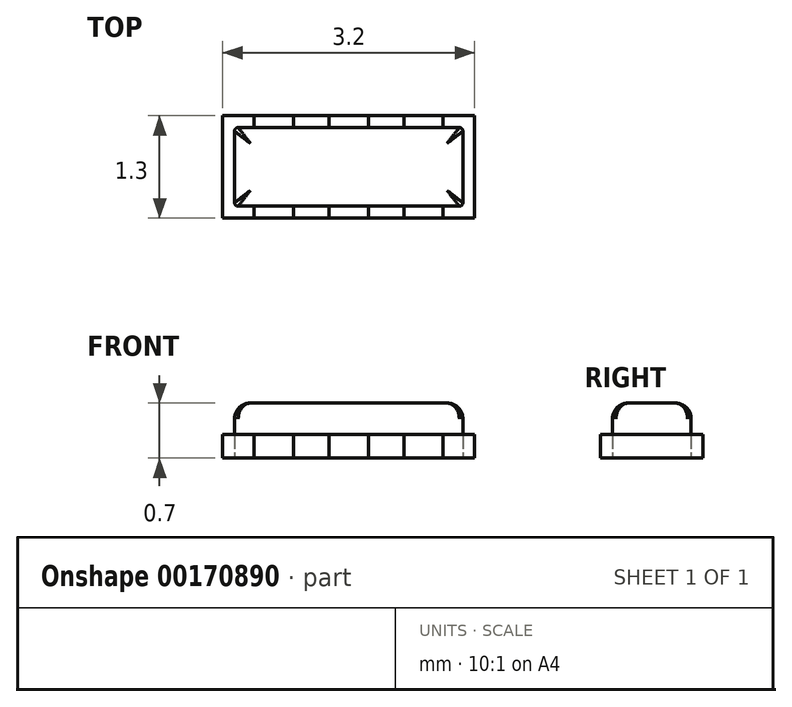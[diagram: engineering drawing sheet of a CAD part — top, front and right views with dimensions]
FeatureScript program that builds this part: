
annotation { "Feature Type Name" : "Feature", "Feature Type Description" : "" }
export const myFeature = defineFeature(function(context is Context, id is Id, definition is map)
    precondition{}
    {
        {
            var Q0;
            Q0=qCreatedBy(makeId("Top.planeOp"),FACE);
            var sketch = newSketch(context, id + "F0", { "sketchPlane" : qUnion([Q0])});
            skLineSegment(sketch, "E0.bottom", {"start": v(-1.6, 0.65) * mm, "end": v(1.6, 0.65) * mm});
            skLineSegment(sketch, "E0.top", {"start": v(-1.6, -0.65) * mm, "end": v(1.6, -0.65) * mm});
            skLineSegment(sketch, "E0.left", {"start": v(-1.6, 0.65) * mm, "end": v(-1.6, -0.65) * mm});
            skLineSegment(sketch, "E0.right", {"start": v(1.6, 0.65) * mm, "end": v(1.6, -0.65) * mm});
            skPoint(sketch, "E0.middle", {"position": v(0, 0) * mm});
            skLineSegment(sketch, "E1.bottom", {"start": v(-1.4, 0.5) * mm, "end": v(1.4, 0.5) * mm});
            skLineSegment(sketch, "E1.top", {"start": v(-1.4, -0.5) * mm, "end": v(1.4, -0.5) * mm});
            skLineSegment(sketch, "E1.left", {"start": v(-1.45, 0.45) * mm, "end": v(-1.45, -0.45) * mm});
            skLineSegment(sketch, "E1.right", {"start": v(1.45, 0.45) * mm, "end": v(1.45, -0.45) * mm});
            skPoint(sketch, "E2.visualSharp", {"position": v(-1.45, 0.5) * mm});
            skArc(sketch, "E2.filletArc", {"start": v(-1.4, 0.5) * mm, "mid": v(-1.44, 0.49) * mm, "end": v(-1.45, 0.45) * mm});
            skPoint(sketch, "E3.visualSharp", {"position": v(-1.45, -0.5) * mm});
            skArc(sketch, "E3.filletArc", {"start": v(-1.45, -0.45) * mm, "mid": v(-1.44, -0.49) * mm, "end": v(-1.4, -0.5) * mm});
            skPoint(sketch, "E4.visualSharp", {"position": v(1.45, -0.5) * mm});
            skArc(sketch, "E4.filletArc", {"start": v(1.4, -0.5) * mm, "mid": v(1.44, -0.49) * mm, "end": v(1.45, -0.45) * mm});
            skPoint(sketch, "E5.visualSharp", {"position": v(1.45, 0.5) * mm});
            skArc(sketch, "E5.filletArc", {"start": v(1.45, 0.45) * mm, "mid": v(1.44, 0.49) * mm, "end": v(1.4, 0.5) * mm});
            skLineSegment(sketch, "E6", {"start": v(-1.2, 0.65) * mm, "end": v(-1.2, -0.65) * mm});
            skLineSegment(sketch, "E7", {"start": v(-0.7, 0.65) * mm, "end": v(-0.7, -0.65) * mm});
            skLineSegment(sketch, "E8", {"start": v(1.2, 0.65) * mm, "end": v(1.2, -0.65) * mm});
            skLineSegment(sketch, "E9", {"start": v(0.7, 0.65) * mm, "end": v(0.7, -0.65) * mm});
            skLineSegment(sketch, "E10", {"start": v(-0.25, 0.65) * mm, "end": v(-0.25, -0.65) * mm});
            skLineSegment(sketch, "E11", {"start": v(0.25, 0.65) * mm, "end": v(0.25, -0.65) * mm});
            skLineSegment(sketch, "E12", {"start": v(-0.7, 0.6) * mm, "end": v(-0.25, 0.6) * mm, "construction": true});
            skLineSegment(sketch, "E13", {"start": v(0.25, 0.6) * mm, "end": v(0.7, 0.6) * mm, "construction": true});
            skSolve(sketch);
        }
        {
            var Q0;
            {var subQ0=sQuery(id+"F0.wireOp",EDGE,"E0.left");Q0=makeQuery(id+"F0.imprint","IMPRINT",FACE,{"disambiguationData":[TD([[makeQuery(id+"F0.imprint","IMPRINT",EDGE,{"derivedFrom":subQ0}),1.0]])]});}
            var Q1;
            {var subQ0=sQuery(id+"F0.wireOp",EDGE,"E7");var subQ1=sQuery(id+"F0.wireOp",EDGE,"E0.bottom");var subQ2=makeQuery(id+"F0.imprint","INTERSECT",VERTEX,{"derivedFrom":[subQ1,subQ0]});Q1=makeQuery(id+"F0.imprint","IMPRINT",FACE,{"disambiguationData":[TD([[makeQuery(id+"F0.imprint","IMPRINT",EDGE,{"disambiguationData":[TD([[subQ2,-1.0]])],"derivedFrom":subQ1}),-1.0]])]});}
            var Q2;
            {var subQ0=sQuery(id+"F0.wireOp",EDGE,"E9");var subQ1=sQuery(id+"F0.wireOp",EDGE,"E0.bottom");var subQ2=makeQuery(id+"F0.imprint","INTERSECT",VERTEX,{"derivedFrom":[subQ1,subQ0]});Q2=makeQuery(id+"F0.imprint","IMPRINT",FACE,{"disambiguationData":[TD([[makeQuery(id+"F0.imprint","IMPRINT",EDGE,{"disambiguationData":[TD([[subQ2,1.0]])],"derivedFrom":subQ1}),-1.0]])]});}
            var Q3;
            {var subQ0=sQuery(id+"F0.wireOp",EDGE,"E0.right");Q3=makeQuery(id+"F0.imprint","IMPRINT",FACE,{"disambiguationData":[TD([[makeQuery(id+"F0.imprint","IMPRINT",EDGE,{"derivedFrom":subQ0}),-1.0]])]});}
            var Q4;
            {var subQ0=sQuery(id+"F0.wireOp",EDGE,"E9");var subQ1=sQuery(id+"F0.wireOp",EDGE,"E0.top");var subQ2=makeQuery(id+"F0.imprint","INTERSECT",VERTEX,{"derivedFrom":[subQ1,subQ0]});Q4=makeQuery(id+"F0.imprint","IMPRINT",FACE,{"disambiguationData":[TD([[makeQuery(id+"F0.imprint","IMPRINT",EDGE,{"disambiguationData":[TD([[subQ2,1.0]])],"derivedFrom":subQ1}),1.0]])]});}
            var Q5;
            {var subQ0=sQuery(id+"F0.wireOp",EDGE,"E7");var subQ1=sQuery(id+"F0.wireOp",EDGE,"E0.top");var subQ2=makeQuery(id+"F0.imprint","INTERSECT",VERTEX,{"derivedFrom":[subQ1,subQ0]});Q5=makeQuery(id+"F0.imprint","IMPRINT",FACE,{"disambiguationData":[TD([[makeQuery(id+"F0.imprint","IMPRINT",EDGE,{"disambiguationData":[TD([[subQ2,-1.0]])],"derivedFrom":subQ1}),1.0]])]});}
            var Q6;
            Q6=makeQuery(id+"F0.imprint","IMPRINT",FACE,{"disambiguationData":[TD([[makeQuery(id+"F0.imprint","IMPRINT",EDGE,{"derivedFrom":sQuery(id+"F0.wireOp",EDGE,"E1.left")}),1.0]])]});
            var Q7;
            {var subQ0=sQuery(id+"F0.wireOp",EDGE,"E7");var subQ1=sQuery(id+"F0.wireOp",EDGE,"E1.bottom");var subQ2=makeQuery(id+"F0.imprint","INTERSECT",VERTEX,{"derivedFrom":[subQ1,subQ0]});Q7=makeQuery(id+"F0.imprint","IMPRINT",FACE,{"disambiguationData":[TD([[makeQuery(id+"F0.imprint","IMPRINT",EDGE,{"disambiguationData":[TD([[subQ2,-1.0]])],"derivedFrom":subQ1}),-1.0]])]});}
            var Q8;
            {var subQ0=sQuery(id+"F0.wireOp",EDGE,"E11");var subQ1=sQuery(id+"F0.wireOp",EDGE,"E1.bottom");var subQ2=makeQuery(id+"F0.imprint","INTERSECT",VERTEX,{"derivedFrom":[subQ1,subQ0]});Q8=makeQuery(id+"F0.imprint","IMPRINT",FACE,{"disambiguationData":[TD([[makeQuery(id+"F0.imprint","IMPRINT",EDGE,{"disambiguationData":[TD([[subQ2,-1.0]])],"derivedFrom":subQ1}),-1.0]])]});}
            var Q9;
            Q9=makeQuery(id+"F0.imprint","IMPRINT",FACE,{"disambiguationData":[TD([[makeQuery(id+"F0.imprint","IMPRINT",EDGE,{"derivedFrom":sQuery(id+"F0.wireOp",EDGE,"E1.right")}),-1.0]])]});
            var Q10;
            {var subQ0=sQuery(id+"F0.wireOp",EDGE,"E6");var subQ1=sQuery(id+"F0.wireOp",EDGE,"E1.bottom");var subQ2=makeQuery(id+"F0.imprint","INTERSECT",VERTEX,{"derivedFrom":[subQ1,subQ0]});Q10=makeQuery(id+"F0.imprint","IMPRINT",FACE,{"disambiguationData":[TD([[makeQuery(id+"F0.imprint","IMPRINT",EDGE,{"disambiguationData":[TD([[subQ2,-1.0]])],"derivedFrom":subQ1}),-1.0]])]});}
            var Q11;
            {var subQ0=sQuery(id+"F0.wireOp",EDGE,"E10");var subQ1=sQuery(id+"F0.wireOp",EDGE,"E1.bottom");var subQ2=makeQuery(id+"F0.imprint","INTERSECT",VERTEX,{"derivedFrom":[subQ1,subQ0]});Q11=makeQuery(id+"F0.imprint","IMPRINT",FACE,{"disambiguationData":[TD([[makeQuery(id+"F0.imprint","IMPRINT",EDGE,{"disambiguationData":[TD([[subQ2,-1.0]])],"derivedFrom":subQ1}),-1.0]])]});}
            var Q12;
            {var subQ0=sQuery(id+"F0.wireOp",EDGE,"E9");var subQ1=sQuery(id+"F0.wireOp",EDGE,"E1.bottom");var subQ2=makeQuery(id+"F0.imprint","INTERSECT",VERTEX,{"derivedFrom":[subQ1,subQ0]});Q12=makeQuery(id+"F0.imprint","IMPRINT",FACE,{"disambiguationData":[TD([[makeQuery(id+"F0.imprint","IMPRINT",EDGE,{"disambiguationData":[TD([[subQ2,-1.0]])],"derivedFrom":subQ1}),-1.0]])]});}
            extrude(context, id + "F1", {"entities" : qUnion([Q0, Q1, Q2, Q3, Q4, Q5, Q6, Q7, Q8, Q9, Q10, Q11, Q12]), "depth" : .3 * mm});
        }
        {
            var Q0;
            {var subQ0=sQuery(id+"F0.wireOp",EDGE,"E6");var subQ1=sQuery(id+"F0.wireOp",EDGE,"E0.top");var subQ2=makeQuery(id+"F0.imprint","INTERSECT",VERTEX,{"derivedFrom":[subQ1,subQ0]});Q0=makeQuery(id+"F0.imprint","IMPRINT",FACE,{"disambiguationData":[TD([[makeQuery(id+"F0.imprint","IMPRINT",EDGE,{"disambiguationData":[TD([[subQ2,-1.0]])],"derivedFrom":subQ1}),1.0]])]});}
            var Q1;
            {var subQ0=sQuery(id+"F0.wireOp",EDGE,"E8");var subQ1=sQuery(id+"F0.wireOp",EDGE,"E0.top");var subQ2=makeQuery(id+"F0.imprint","INTERSECT",VERTEX,{"derivedFrom":[subQ1,subQ0]});Q1=makeQuery(id+"F0.imprint","IMPRINT",FACE,{"disambiguationData":[TD([[makeQuery(id+"F0.imprint","IMPRINT",EDGE,{"disambiguationData":[TD([[subQ2,1.0]])],"derivedFrom":subQ1}),1.0]])]});}
            var Q2;
            {var subQ0=sQuery(id+"F0.wireOp",EDGE,"E8");var subQ1=sQuery(id+"F0.wireOp",EDGE,"E0.bottom");var subQ2=makeQuery(id+"F0.imprint","INTERSECT",VERTEX,{"derivedFrom":[subQ1,subQ0]});Q2=makeQuery(id+"F0.imprint","IMPRINT",FACE,{"disambiguationData":[TD([[makeQuery(id+"F0.imprint","IMPRINT",EDGE,{"disambiguationData":[TD([[subQ2,1.0]])],"derivedFrom":subQ1}),-1.0]])]});}
            var Q3;
            {var subQ0=sQuery(id+"F0.wireOp",EDGE,"E10");var subQ1=sQuery(id+"F0.wireOp",EDGE,"E0.bottom");var subQ2=makeQuery(id+"F0.imprint","INTERSECT",VERTEX,{"derivedFrom":[subQ1,subQ0]});Q3=makeQuery(id+"F0.imprint","IMPRINT",FACE,{"disambiguationData":[TD([[makeQuery(id+"F0.imprint","IMPRINT",EDGE,{"disambiguationData":[TD([[subQ2,-1.0]])],"derivedFrom":subQ1}),-1.0]])]});}
            var Q4;
            {var subQ0=sQuery(id+"F0.wireOp",EDGE,"E6");var subQ1=sQuery(id+"F0.wireOp",EDGE,"E0.bottom");var subQ2=makeQuery(id+"F0.imprint","INTERSECT",VERTEX,{"derivedFrom":[subQ1,subQ0]});Q4=makeQuery(id+"F0.imprint","IMPRINT",FACE,{"disambiguationData":[TD([[makeQuery(id+"F0.imprint","IMPRINT",EDGE,{"disambiguationData":[TD([[subQ2,-1.0]])],"derivedFrom":subQ1}),-1.0]])]});}
            var Q5;
            {var subQ0=sQuery(id+"F0.wireOp",EDGE,"E10");var subQ1=sQuery(id+"F0.wireOp",EDGE,"E0.top");var subQ2=makeQuery(id+"F0.imprint","INTERSECT",VERTEX,{"derivedFrom":[subQ1,subQ0]});Q5=makeQuery(id+"F0.imprint","IMPRINT",FACE,{"disambiguationData":[TD([[makeQuery(id+"F0.imprint","IMPRINT",EDGE,{"disambiguationData":[TD([[subQ2,-1.0]])],"derivedFrom":subQ1}),1.0]])]});}
            extrude(context, id + "F2", {"entities" : qUnion([Q0, Q1, Q2, Q3, Q4, Q5]), "depth" : .3 * mm});
        }
        {
            var Q0;
            Q0=makeQuery(id+"F0.imprint","IMPRINT",FACE,{"disambiguationData":[TD([[makeQuery(id+"F0.imprint","IMPRINT",EDGE,{"derivedFrom":sQuery(id+"F0.wireOp",EDGE,"E1.right")}),-1.0]])]});
            var Q1;
            {var subQ0=sQuery(id+"F0.wireOp",EDGE,"E9");var subQ1=sQuery(id+"F0.wireOp",EDGE,"E1.bottom");var subQ2=makeQuery(id+"F0.imprint","INTERSECT",VERTEX,{"derivedFrom":[subQ1,subQ0]});Q1=makeQuery(id+"F0.imprint","IMPRINT",FACE,{"disambiguationData":[TD([[makeQuery(id+"F0.imprint","IMPRINT",EDGE,{"disambiguationData":[TD([[subQ2,-1.0]])],"derivedFrom":subQ1}),-1.0]])]});}
            var Q2;
            {var subQ0=sQuery(id+"F0.wireOp",EDGE,"E11");var subQ1=sQuery(id+"F0.wireOp",EDGE,"E1.bottom");var subQ2=makeQuery(id+"F0.imprint","INTERSECT",VERTEX,{"derivedFrom":[subQ1,subQ0]});Q2=makeQuery(id+"F0.imprint","IMPRINT",FACE,{"disambiguationData":[TD([[makeQuery(id+"F0.imprint","IMPRINT",EDGE,{"disambiguationData":[TD([[subQ2,-1.0]])],"derivedFrom":subQ1}),-1.0]])]});}
            var Q3;
            {var subQ0=sQuery(id+"F0.wireOp",EDGE,"E10");var subQ1=sQuery(id+"F0.wireOp",EDGE,"E1.bottom");var subQ2=makeQuery(id+"F0.imprint","INTERSECT",VERTEX,{"derivedFrom":[subQ1,subQ0]});Q3=makeQuery(id+"F0.imprint","IMPRINT",FACE,{"disambiguationData":[TD([[makeQuery(id+"F0.imprint","IMPRINT",EDGE,{"disambiguationData":[TD([[subQ2,-1.0]])],"derivedFrom":subQ1}),-1.0]])]});}
            var Q4;
            {var subQ0=sQuery(id+"F0.wireOp",EDGE,"E7");var subQ1=sQuery(id+"F0.wireOp",EDGE,"E1.bottom");var subQ2=makeQuery(id+"F0.imprint","INTERSECT",VERTEX,{"derivedFrom":[subQ1,subQ0]});Q4=makeQuery(id+"F0.imprint","IMPRINT",FACE,{"disambiguationData":[TD([[makeQuery(id+"F0.imprint","IMPRINT",EDGE,{"disambiguationData":[TD([[subQ2,-1.0]])],"derivedFrom":subQ1}),-1.0]])]});}
            var Q5;
            {var subQ0=sQuery(id+"F0.wireOp",EDGE,"E6");var subQ1=sQuery(id+"F0.wireOp",EDGE,"E1.bottom");var subQ2=makeQuery(id+"F0.imprint","INTERSECT",VERTEX,{"derivedFrom":[subQ1,subQ0]});Q5=makeQuery(id+"F0.imprint","IMPRINT",FACE,{"disambiguationData":[TD([[makeQuery(id+"F0.imprint","IMPRINT",EDGE,{"disambiguationData":[TD([[subQ2,-1.0]])],"derivedFrom":subQ1}),-1.0]])]});}
            var Q6;
            Q6=makeQuery(id+"F0.imprint","IMPRINT",FACE,{"disambiguationData":[TD([[makeQuery(id+"F0.imprint","IMPRINT",EDGE,{"derivedFrom":sQuery(id+"F0.wireOp",EDGE,"E1.left")}),1.0]])]});
            extrude(context, id + "F3", {"entities" : qUnion([Q0, Q1, Q2, Q3, Q4, Q5, Q6]), "depth" : .7 * mm});
        }
        {
            var Q0;
            Q0=makeQuery(id+"F3.opExtrude","CAP_EDGE",EDGE,{"disambiguationData":[OSD([sQuery(id+"F0.wireOp",EDGE,"E1.left")])],"isStart":false});
            var Q1;
            Q1=makeQuery(id+"F3.opExtrude","CAP_EDGE",EDGE,{"disambiguationData":[OSD([sQuery(id+"F0.wireOp",EDGE,"E1.top")])],"isStart":false});
            var Q2;
            Q2=makeQuery(id+"F3.opExtrude","CAP_EDGE",EDGE,{"disambiguationData":[OSD([sQuery(id+"F0.wireOp",EDGE,"E3.filletArc")])],"isStart":false});
            var Q3;
            Q3=makeQuery(id+"F3.opExtrude","CAP_EDGE",EDGE,{"disambiguationData":[OSD([sQuery(id+"F0.wireOp",EDGE,"E4.filletArc")])],"isStart":false});
            var Q4;
            Q4=makeQuery(id+"F3.opExtrude","CAP_EDGE",EDGE,{"disambiguationData":[OSD([sQuery(id+"F0.wireOp",EDGE,"E1.right")])],"isStart":false});
            var Q5;
            Q5=makeQuery(id+"F3.opExtrude","CAP_EDGE",EDGE,{"disambiguationData":[OSD([sQuery(id+"F0.wireOp",EDGE,"E5.filletArc")])],"isStart":false});
            var Q6;
            Q6=makeQuery(id+"F3.opExtrude","CAP_EDGE",EDGE,{"disambiguationData":[OSD([sQuery(id+"F0.wireOp",EDGE,"E1.bottom")])],"isStart":false});
            var Q7;
            Q7=makeQuery(id+"F3.opExtrude","CAP_EDGE",EDGE,{"disambiguationData":[OSD([sQuery(id+"F0.wireOp",EDGE,"E2.filletArc")])],"isStart":false});
            fillet(context, id + "F4", {"entities" : qUnion([Q0, Q1, Q2, Q3, Q4, Q5, Q6, Q7]), "radius" : 0.2 * mm, "allowEdgeOverflow" : false});
        }
    });
